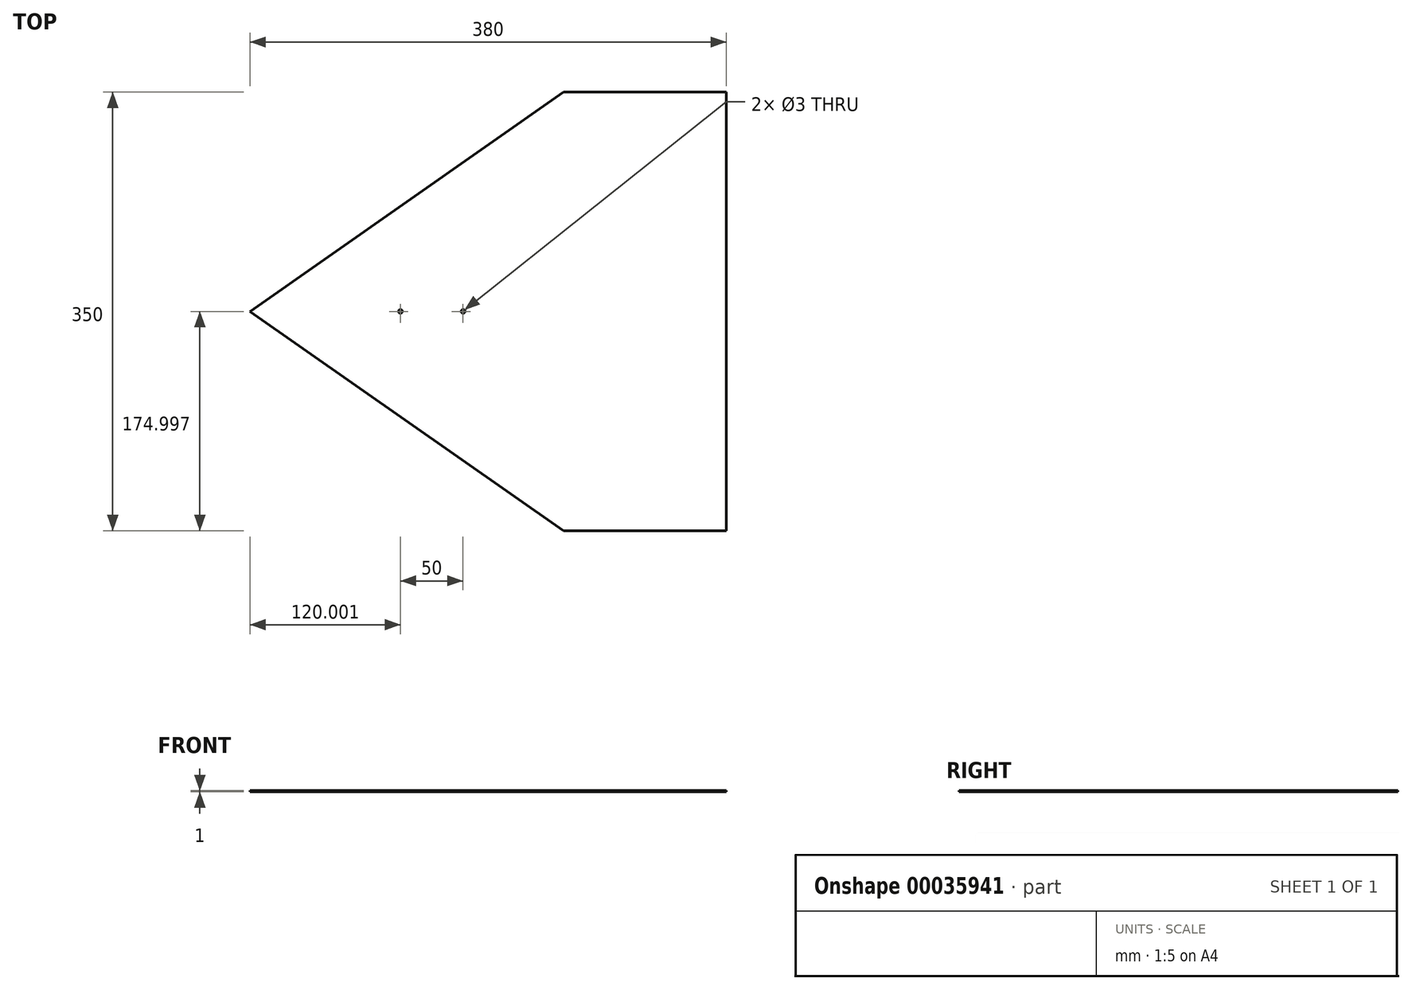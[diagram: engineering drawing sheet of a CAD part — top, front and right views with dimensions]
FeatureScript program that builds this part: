
annotation { "Feature Type Name" : "Feature", "Feature Type Description" : "" }
export const myFeature = defineFeature(function(context is Context, id is Id, definition is map)
    precondition{}
    {
        {
            var Q0;
            Q0=qCreatedBy(makeId("Top.planeOp"),FACE);
            var sketch = newSketch(context, id + "F0", { "sketchPlane" : qUnion([Q0])});
            skLineSegment(sketch, "E0.bottom", {"start": v(47.94, 169.1) * mm, "end": v(177.94, 169.1) * mm});
            skLineSegment(sketch, "E0.top", {"start": v(47.94, -180.9) * mm, "end": v(177.94, -180.9) * mm});
            skLineSegment(sketch, "E0.right", {"start": v(177.94, 169.1) * mm, "end": v(177.94, -180.9) * mm});
            skLineSegment(sketch, "E1", {"start": v(47.94, 186.91) * mm, "end": v(47.94, -197.7) * mm, "construction": true});
            skLineSegment(sketch, "E2", {"start": v(-257.43, -5.9) * mm, "end": v(302, -5.9) * mm, "construction": true});
            skLineSegment(sketch, "E3", {"start": v(-32.06, 24.43) * mm, "end": v(-32.06, -21.84) * mm, "construction": true});
            skLineSegment(sketch, "E4", {"start": v(-82.06, 24.43) * mm, "end": v(-82.06, -15.67) * mm, "construction": true});
            skCircle(sketch, "E5", {"center": v(-82.06, -5.9) * mm, "radius": 1.5 * mm});
            skCircle(sketch, "E6", {"center": v(-32.06, -5.9) * mm, "radius": 1.5 * mm});
            skLineSegment(sketch, "E7", {"start": v(-202.06, -5.9) * mm, "end": v(47.94, 169.1) * mm});
            skLineSegment(sketch, "E8", {"start": v(-202.06, -5.9) * mm, "end": v(47.94, -180.9) * mm});
            skPoint(sketch, "E9.orphan", {"position": v(-202.06, 169.1) * mm});
            skPoint(sketch, "E10.orphan", {"position": v(-202.06, -180.9) * mm});
            skSolve(sketch);
        }
        {
            var Q0;
            Q0 = qSketchRegion(id + "F0", true);
            extrude(context, id + "F1", {"entities" : qUnion([Q0]), "depth" : 1 * mm});
        }
    });
